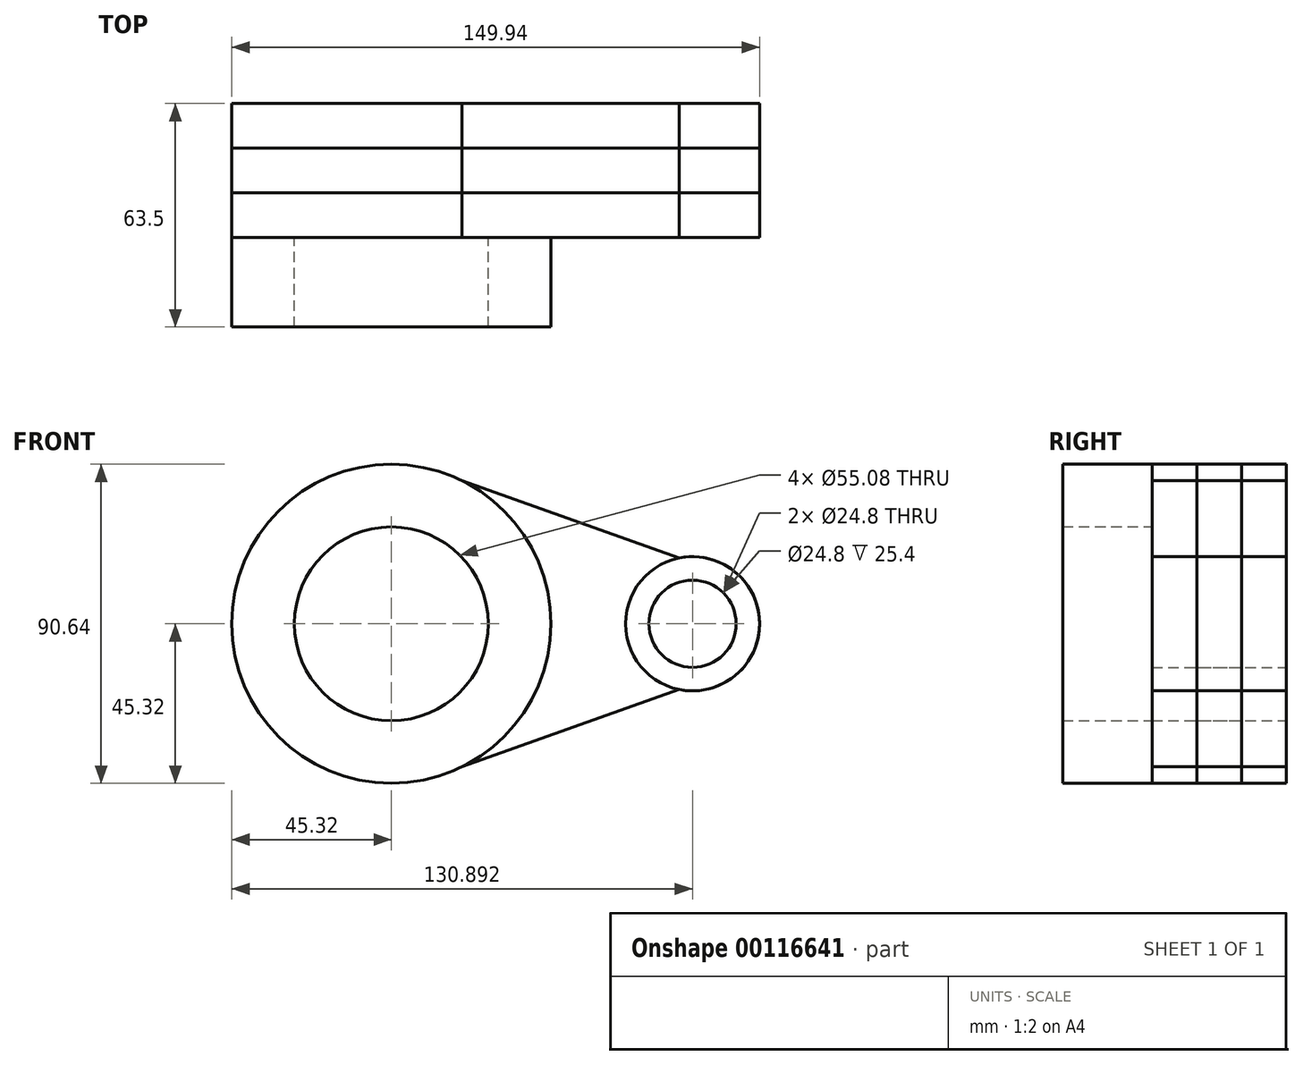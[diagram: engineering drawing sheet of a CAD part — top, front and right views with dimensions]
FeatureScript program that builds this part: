
annotation { "Feature Type Name" : "Feature", "Feature Type Description" : "" }
export const myFeature = defineFeature(function(context is Context, id is Id, definition is map)
    precondition{}
    {
        {
            var Q0;
            Q0=qCreatedBy(makeId("Front.planeOp"),FACE);
            var sketch = newSketch(context, id + "F0", { "sketchPlane" : qUnion([Q0])});
            skCircle(sketch, "E0", {"center": v(0, 0) * mm, "radius": 45.32 * mm});
            skCircle(sketch, "E1", {"center": v(85.57, 0) * mm, "radius": 19.05 * mm});
            skLineSegment(sketch, "E2", {"start": v(20.1, 40.62) * mm, "end": v(81.79, 18.67) * mm});
            skLineSegment(sketch, "E3", {"start": v(85.57, 0) * mm, "end": v(85.57, -40.65) * mm});
            skCircle(sketch, "E4", {"center": v(85.57, 0) * mm, "radius": 12.4 * mm});
            skCircle(sketch, "E5", {"center": v(0, 0) * mm, "radius": 27.54 * mm});
            skLineSegment(sketch, "E6.bottom", {"start": v(19.05, 4.76) * mm, "end": v(-19.05, 4.76) * mm});
            skLineSegment(sketch, "E6.top", {"start": v(19.05, -4.76) * mm, "end": v(-19.05, -4.76) * mm});
            skLineSegment(sketch, "E6.left", {"start": v(19.05, 4.76) * mm, "end": v(19.05, -4.76) * mm});
            skLineSegment(sketch, "E6.right", {"start": v(-19.05, 4.76) * mm, "end": v(-19.05, -4.76) * mm});
            skLineSegment(sketch, "E7", {"start": v(20.1, -40.62) * mm, "end": v(81.79, -18.67) * mm});
            skSolve(sketch);
        }
        {
            var Q0;
            Q0=makeQuery(id+"F0.imprint","IMPRINT",FACE,{"disambiguationData":[TD([[makeQuery(id+"F0.imprint","IMPRINT",EDGE,{"derivedFrom":sQuery(id+"F0.wireOp",EDGE,"E5")}),-1.0]])]});
            var Q1;
            Q1=makeQuery(id+"F0.imprint","IMPRINT",FACE,{"disambiguationData":[TD([[makeQuery(id+"F0.imprint","IMPRINT",EDGE,{"derivedFrom":sQuery(id+"F0.wireOp",EDGE,"E4")}),-1.0]])]});
            extrude(context, id + "F1", {"entities" : qUnion([Q0, Q1]), "depth" : 25.4 * mm});
        }
        {
            var Q0;
            Q0 = qSketchRegion(id + "F0", true);
            extrude(context, id + "F2", {"entities" : qUnion([Q0]), "endBound" : BoundingType.SYMMETRIC, "depth" : 25.4 * mm});
        }
        {
            var Q0;
            Q0 = qSketchRegion(id + "F0", true);
            var Q1;
            Q1=makeQuery(id+"F1.opExtrude","CAP_FACE",FACE,{"disambiguationData":[OSD([sQuery(id+"F0.wireOp",EDGE,"E0"),sQuery(id+"F0.wireOp",EDGE,"E5")])],"isStart":false});
            extrude(context, id + "F3", {"entities" : qUnion([Q0, Q1]), "depth" : 25.4 * mm});
        }
    });
